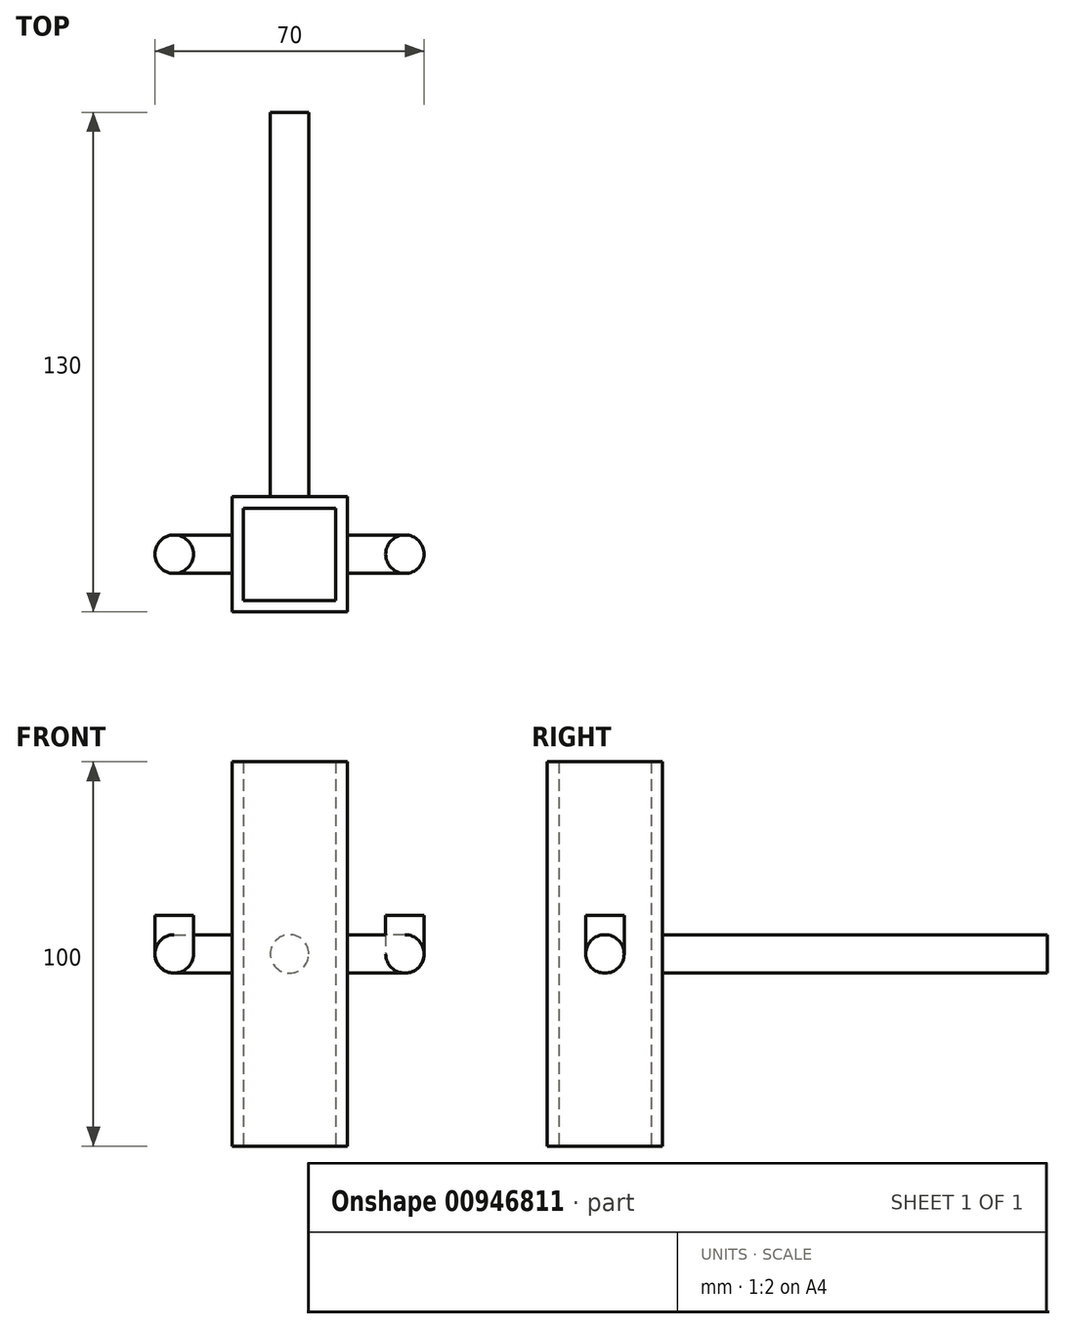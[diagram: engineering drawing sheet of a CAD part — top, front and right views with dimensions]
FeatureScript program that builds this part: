
annotation { "Feature Type Name" : "Feature", "Feature Type Description" : "" }
export const myFeature = defineFeature(function(context is Context, id is Id, definition is map)
    precondition{}
    {
        {
            var Q0;
            Q0=qCreatedBy(makeId("Top.planeOp"),FACE);
            var sketch = newSketch(context, id + "F0", { "sketchPlane" : qUnion([Q0])});
            skLineSegment(sketch, "E0.bottom", {"start": v(-15, 15) * mm, "end": v(15, 15) * mm});
            skLineSegment(sketch, "E0.top", {"start": v(-15, -15) * mm, "end": v(15, -15) * mm});
            skLineSegment(sketch, "E0.left", {"start": v(-15, 15) * mm, "end": v(-15, -15) * mm});
            skLineSegment(sketch, "E0.right", {"start": v(15, 15) * mm, "end": v(15, -15) * mm});
            skLineSegment(sketch, "E1.bottom", {"start": v(-12, 12) * mm, "end": v(12, 12) * mm});
            skLineSegment(sketch, "E1.top", {"start": v(-12, -12) * mm, "end": v(12, -12) * mm});
            skLineSegment(sketch, "E1.left", {"start": v(-12, 12) * mm, "end": v(-12, -12) * mm});
            skLineSegment(sketch, "E1.right", {"start": v(12, 12) * mm, "end": v(12, -12) * mm});
            skSolve(sketch);
        }
        {
            var Q0;
            Q0=makeQuery(id+"F0.imprint","IMPRINT",FACE,{"disambiguationData":[TD([[makeQuery(id+"F0.imprint","IMPRINT",EDGE,{"derivedFrom":sQuery(id+"F0.wireOp",EDGE,"E0.bottom")}),-1.0]])]});
            extrude(context, id + "F1", {"entities" : qUnion([Q0]), "depth" : 100 * mm, "offsetDistance" : 25 * mm});
        }
        {
            var Q0;
            Q0=makeQuery(id+"F1.opExtrude","SWEPT_FACE",FACE,{"disambiguationData":[OSD([sQuery(id+"F0.wireOp",EDGE,"E0.right")])]});
            var sketch = newSketch(context, id + "F2", { "sketchPlane" : qUnion([Q0])});
            skCircle(sketch, "E2", {"center": v(0, 50) * mm, "radius": 5 * mm});
            skSolve(sketch);
        }
        {
            var Q0;
            Q0=makeQuery(id+"F2.imprint","IMPRINT",FACE,{"disambiguationData":[TD([[makeQuery(id+"F2.imprint","IMPRINT",EDGE,{"derivedFrom":sQuery(id+"F2.wireOp",EDGE,"E2")}),1.0]])]});
            extrude(context, id + "F3", {"entities" : qUnion([Q0]), "depth" : 20 * mm, "offsetDistance" : 25 * mm});
        }
        {
            var Q0;
            Q0=qCreatedBy(makeId("Top.planeOp"),FACE);
            cPlane(context, id + "F4", {"entities" : qUnion([Q0]), "cplaneType" : CPlaneType.OFFSET, "offset" : 55 * mm, "width" : 150 * mm, "height" : 150 * mm});
        }
        {
            var Q0;
            Q0=qCreatedBy(id+"F4.planeOp",FACE);
            var sketch = newSketch(context, id + "F5", { "sketchPlane" : qUnion([Q0])});
            skCircle(sketch, "E3", {"center": v(30, 0) * mm, "radius": 5 * mm});
            skSolve(sketch);
        }
        {
            var Q0;
            Q0 = qSketchRegion(id + "F5", true);
            extrude(context, id + "F6", {"entities" : qUnion([Q0]), "depth" : 5 * mm, "offsetDistance" : 25 * mm, "hasSecondDirection" : true, "secondDirectionOppositeDirection" : true, "secondDirectionDepth" : 10 * mm});
        }
        {
            var Q0;
            Q0=makeQuery(id+"F3.opExtrude","CAP_EDGE",EDGE,{"disambiguationData":[OSD([sQuery(id+"F2.wireOp",EDGE,"E2")])],"isStart":false});
            var Q1;
            Q1=makeQuery(id+"F6.opExtrude","CAP_EDGE",EDGE,{"disambiguationData":[OSD([sQuery(id+"F5.wireOp",EDGE,"E3")])],"isStart":true});
            fillet(context, id + "F7", {"entities" : qUnion([Q0, Q1]), "radius" : 5 * mm, "tangentPropagation" : true, "allowEdgeOverflow" : false});
        }
        {
            var Q0;
            Q0=makeQuery(id+"F6.opExtrude","SWEPT_BODY",BODY,{"disambiguationData":[OSD([sQuery(id+"F5.wireOp",EDGE,"E3")])]});
            var Q1;
            Q1=makeQuery(id+"F3.opExtrude","SWEPT_BODY",BODY,{"disambiguationData":[OSD([sQuery(id+"F2.wireOp",EDGE,"E2")])]});
            var Q2;
            Q2=makeQuery(id+"F1.opExtrude","SWEPT_FACE",FACE,{"disambiguationData":[OSD([sQuery(id+"F0.wireOp",EDGE,"E0.left")])]});
            mirror(context, id + "F8", {"entities" : qUnion([Q0, Q1]), "mirrorPlane" : qUnion([Q2])});
        }
        {
            var Q0;
            Q0=makeQuery(id+"F8.opPattern","COPY",BODY,{"derivedFrom":makeQuery(id+"F6.opExtrude","SWEPT_BODY",BODY,{"disambiguationData":[OSD([sQuery(id+"F5.wireOp",EDGE,"E3")])]}),"instanceName":"1"});
            var Q1;
            Q1=makeQuery(id+"F8.opPattern","COPY",BODY,{"derivedFrom":makeQuery(id+"F3.opExtrude","SWEPT_BODY",BODY,{"disambiguationData":[OSD([sQuery(id+"F2.wireOp",EDGE,"E2")])]}),"instanceName":"1"});
            transform(context, id + "F9", {"entities" : qUnion([Q0, Q1]), "transformType" : TransformType.TRANSLATION_3D, "dx" : 30 * mm, "dy" : 0 * mm, "dz" : 0 * mm, "makeCopy" : false});
        }
        {
            var Q0;
            Q0=makeQuery(id+"F1.opExtrude","SWEPT_FACE",FACE,{"disambiguationData":[OSD([sQuery(id+"F0.wireOp",EDGE,"E0.bottom")])]});
            var sketch = newSketch(context, id + "F10", { "sketchPlane" : qUnion([Q0])});
            skCircle(sketch, "E4", {"center": v(0, 50) * mm, "radius": 5 * mm});
            skSolve(sketch);
        }
        {
            var Q0;
            Q0=makeQuery(id+"F10.imprint","IMPRINT",FACE,{"disambiguationData":[TD([[makeQuery(id+"F10.imprint","IMPRINT",EDGE,{"derivedFrom":sQuery(id+"F10.wireOp",EDGE,"E4")}),1.0]])]});
            extrude(context, id + "F11", {"entities" : qUnion([Q0]), "operationType" : NewBodyOperationType.ADD, "depth" : 100 * mm, "offsetDistance" : 25 * mm});
        }
    });
